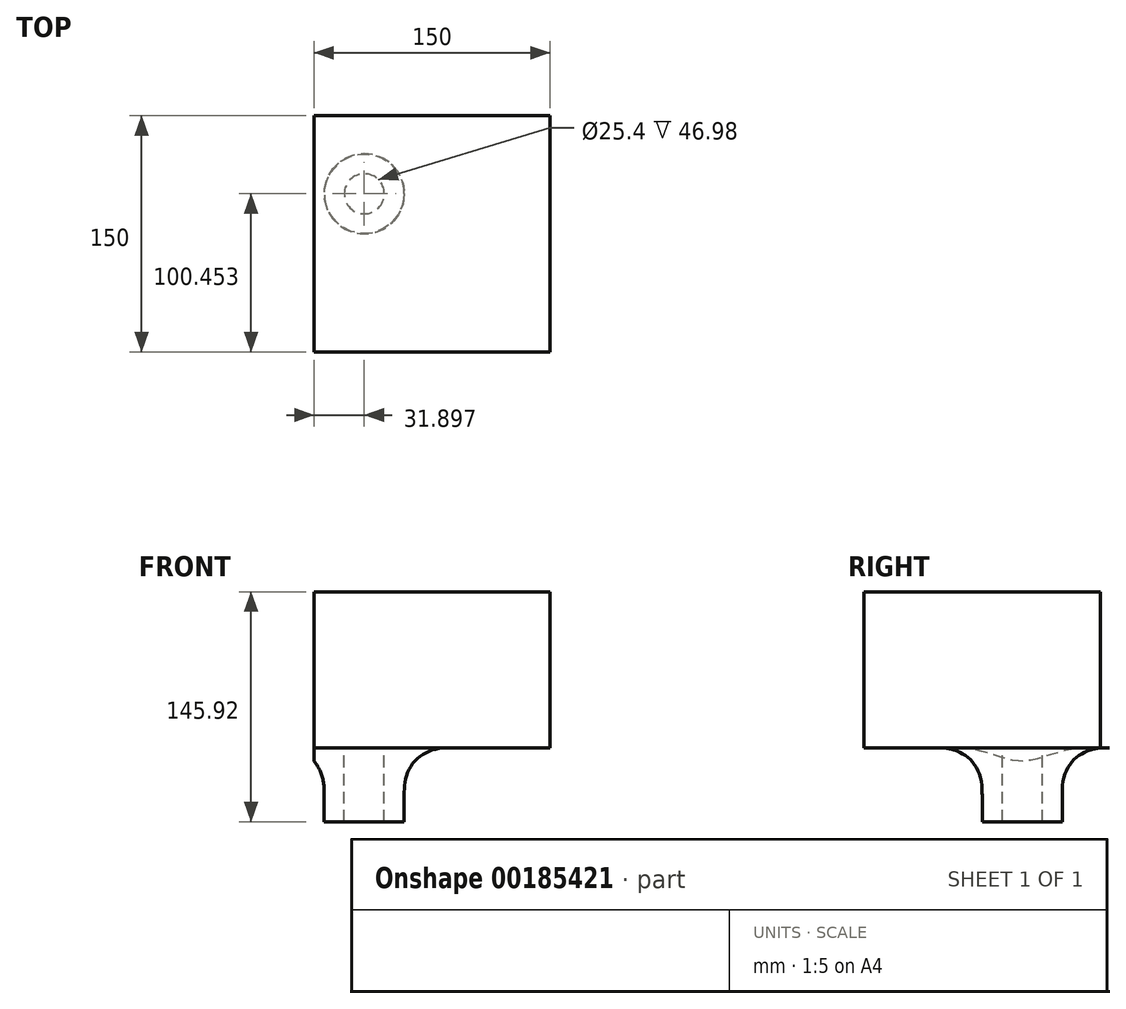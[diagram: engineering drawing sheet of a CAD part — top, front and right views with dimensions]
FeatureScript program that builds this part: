
annotation { "Feature Type Name" : "Feature", "Feature Type Description" : "" }
export const myFeature = defineFeature(function(context is Context, id is Id, definition is map)
    precondition{}
    {
        {
            var Q0;
            Q0=qCreatedBy(makeId("Front.planeOp"),FACE);
            var sketch = newSketch(context, id + "F0", { "sketchPlane" : qUnion([Q0])});
            skLineSegment(sketch, "E0.bottom", {"start": v(0, 95.92) * mm, "end": v(150, 95.92) * mm});
            skLineSegment(sketch, "E0.top", {"start": v(0, -3.02) * mm, "end": v(150, -3.02) * mm});
            skLineSegment(sketch, "E0.left", {"start": v(0, 95.92) * mm, "end": v(0, -3.02) * mm});
            skLineSegment(sketch, "E0.right", {"start": v(150, 95.92) * mm, "end": v(150, -3.02) * mm});
            skSolve(sketch);
        }
        {
            var Q0;
            Q0=makeQuery(id+"F0.imprint","IMPRINT",FACE,{"disambiguationData":[TD([[makeQuery(id+"F0.imprint","IMPRINT",EDGE,{"derivedFrom":sQuery(id+"F0.wireOp",EDGE,"E0.bottom")}),-1.0]])]});
            extrude(context, id + "F1", {"entities" : qUnion([Q0]), "offsetDistance" : 25 * mm, "depth" : 150 * mm});
        }
        {
            var Q0;
            Q0=qCreatedBy(makeId("Top.planeOp"),FACE);
            var sketch = newSketch(context, id + "F2", { "sketchPlane" : qUnion([Q0])});
            skCircle(sketch, "E1", {"center": v(31.9, -49.55) * mm, "radius": 12.7 * mm});
            skCircle(sketch, "E2", {"center": v(31.9, -49.55) * mm, "radius": 25.4 * mm});
            skSolve(sketch);
        }
        {
            var Q0;
            Q0 = qSketchRegion(id + "F2", true);
            extrude(context, id + "F3", {"entities" : qUnion([Q0]), "operationType" : NewBodyOperationType.ADD, "oppositeDirection" : true, "offsetDistance" : 25 * mm, "depth" : 50 * mm});
        }
        {
            var Q0;
            Q0=makeQuery(id+"F3.boolean.opBoolean","INTERSECT",EDGE,{"derivedFrom":[makeQuery(id+"F1.opExtrude","SWEPT_FACE",FACE,{"disambiguationData":[OSD([sQuery(id+"F0.wireOp",EDGE,"E0.top")])]}),makeQuery(id+"F3.opExtrude","SWEPT_FACE",FACE,{"disambiguationData":[OSD([sQuery(id+"F2.wireOp",EDGE,"E2")])]})]});
            fillet(context, id + "F4", {"entities" : qUnion([Q0]), "radius" : 30 * mm, "tangentPropagation" : true, "crossSection" : FilletCrossSection.CURVATURE, "magnitude" : 0.5, "defaultsChanged" : true, "vertexSettings" : []});
        }
    });
